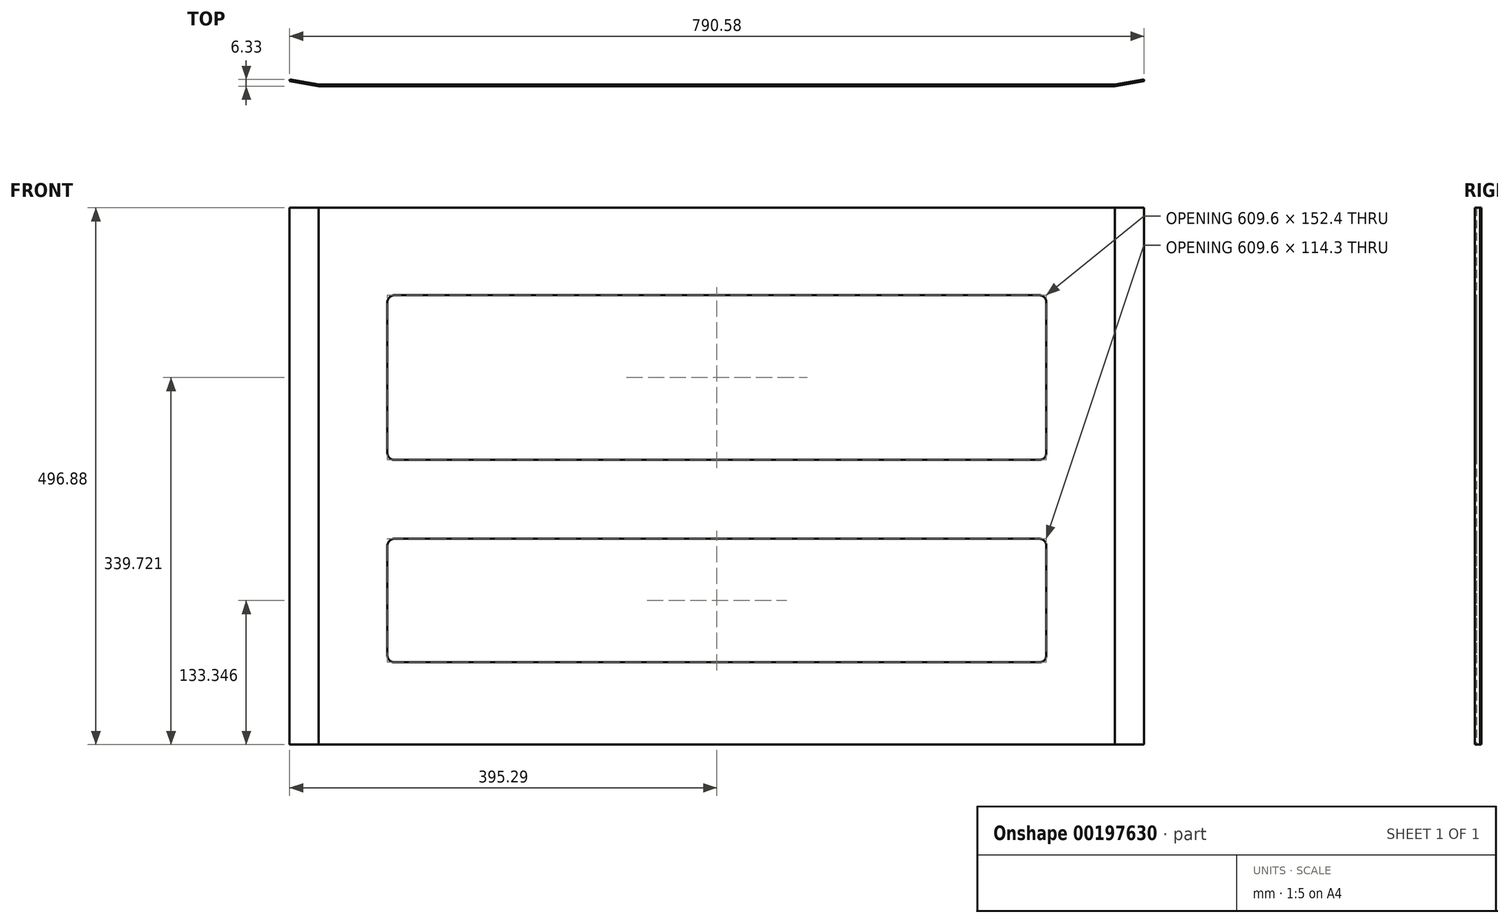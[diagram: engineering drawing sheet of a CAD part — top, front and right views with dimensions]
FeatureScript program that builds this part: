
annotation { "Feature Type Name" : "Feature", "Feature Type Description" : "" }
export const myFeature = defineFeature(function(context is Context, id is Id, definition is map)
    precondition{}
    {
        {
            var Q0;
            Q0=qCreatedBy(makeId("Front.planeOp"),FACE);
            var sketch = newSketch(context, id + "F0", { "sketchPlane" : qUnion([Q0])});
            skLineSegment(sketch, "E0.bottom", {"start": v(395.29, 248.44) * mm, "end": v(-395.29, 248.44) * mm});
            skLineSegment(sketch, "E0.top", {"start": v(395.29, -248.44) * mm, "end": v(-395.29, -248.44) * mm});
            skLineSegment(sketch, "E0.left", {"start": v(395.29, 248.44) * mm, "end": v(395.29, -248.44) * mm});
            skLineSegment(sketch, "E0.right", {"start": v(-395.29, 248.44) * mm, "end": v(-395.29, -248.44) * mm});
            skPoint(sketch, "E0.middle", {"position": v(0, 0) * mm});
            skLineSegment(sketch, "E1.bottom", {"start": v(298.45, 167.48) * mm, "end": v(-298.45, 167.48) * mm});
            skLineSegment(sketch, "E1.top", {"start": v(298.45, 15.08) * mm, "end": v(-298.45, 15.08) * mm});
            skLineSegment(sketch, "E1.left", {"start": v(304.8, 161.13) * mm, "end": v(304.8, 21.43) * mm});
            skLineSegment(sketch, "E1.right", {"start": v(-304.8, 161.13) * mm, "end": v(-304.8, 21.43) * mm});
            skPoint(sketch, "E1.middle", {"position": v(0, 91.28) * mm});
            skLineSegment(sketch, "E2.bottom", {"start": v(298.45, -57.94) * mm, "end": v(-298.45, -57.94) * mm});
            skLineSegment(sketch, "E2.top", {"start": v(298.45, -172.24) * mm, "end": v(-298.45, -172.24) * mm});
            skLineSegment(sketch, "E2.left", {"start": v(304.8, -64.3) * mm, "end": v(304.8, -165.9) * mm});
            skLineSegment(sketch, "E2.right", {"start": v(-304.8, -64.3) * mm, "end": v(-304.8, -165.9) * mm});
            skPoint(sketch, "E2.middle", {"position": v(0, -115.1) * mm});
            skPoint(sketch, "E3.visualSharp", {"position": v(304.8, 167.48) * mm});
            skArc(sketch, "E3.filletArc", {"start": v(304.8, 161.13) * mm, "mid": v(302.94, 165.62) * mm, "end": v(298.45, 167.48) * mm});
            skPoint(sketch, "E4.visualSharp", {"position": v(-304.8, 167.48) * mm});
            skArc(sketch, "E4.filletArc", {"start": v(-298.45, 167.48) * mm, "mid": v(-302.94, 165.62) * mm, "end": v(-304.8, 161.13) * mm});
            skPoint(sketch, "E5.visualSharp", {"position": v(-304.8, 15.08) * mm});
            skArc(sketch, "E5.filletArc", {"start": v(-304.8, 21.43) * mm, "mid": v(-302.94, 16.94) * mm, "end": v(-298.45, 15.08) * mm});
            skPoint(sketch, "E6.visualSharp", {"position": v(304.8, 15.08) * mm});
            skArc(sketch, "E6.filletArc", {"start": v(298.45, 15.08) * mm, "mid": v(302.94, 16.94) * mm, "end": v(304.8, 21.43) * mm});
            skPoint(sketch, "E7.visualSharp", {"position": v(304.8, -57.94) * mm});
            skArc(sketch, "E7.filletArc", {"start": v(304.8, -64.3) * mm, "mid": v(302.94, -59.8) * mm, "end": v(298.45, -57.94) * mm});
            skPoint(sketch, "E8.visualSharp", {"position": v(304.8, -172.24) * mm});
            skArc(sketch, "E8.filletArc", {"start": v(298.45, -172.24) * mm, "mid": v(302.94, -170.38) * mm, "end": v(304.8, -165.9) * mm});
            skPoint(sketch, "E9.visualSharp", {"position": v(-304.8, -57.94) * mm});
            skArc(sketch, "E9.filletArc", {"start": v(-298.45, -57.94) * mm, "mid": v(-302.94, -59.8) * mm, "end": v(-304.8, -64.3) * mm});
            skPoint(sketch, "E10.visualSharp", {"position": v(-304.8, -172.24) * mm});
            skArc(sketch, "E10.filletArc", {"start": v(-304.8, -165.9) * mm, "mid": v(-302.94, -170.38) * mm, "end": v(-298.45, -172.24) * mm});
            skSolve(sketch);
        }
        {
            var Q0;
            Q0=makeQuery(id+"F0.imprint","IMPRINT",FACE,{"disambiguationData":[TD([[makeQuery(id+"F0.imprint","IMPRINT",EDGE,{"derivedFrom":sQuery(id+"F0.wireOp",EDGE,"E0.bottom")}),1.0]])]});
            extrude(context, id + "F1", {"entities" : qUnion([Q0]), "oppositeDirection" : true, "depth" : 76.2 * mm, "offsetDistance" : 25.4 * mm});
        }
        {
            var Q0;
            Q0=makeQuery(id+"F1.opExtrude","CAP_EDGE",EDGE,{"disambiguationData":[OSD([sQuery(id+"F0.wireOp",EDGE,"E0.right")])],"isStart":true});
            var Q1;
            Q1=makeQuery(id+"F1.opExtrude","CAP_EDGE",EDGE,{"disambiguationData":[OSD([sQuery(id+"F0.wireOp",EDGE,"E0.left")])],"isStart":true});
            chamfer(context, id + "F2", {"entities" : qUnion([Q0, Q1]), "chamferType" : ChamferType.TWO_OFFSETS, "width1" : 26.99 * mm, "oppositeDirection" : false, "width2" : 4.76 * mm, "tangentPropagation" : true});
        }
        {
            var Q0;
            Q0=qCreatedBy(makeId("Top.planeOp"),FACE);
            var sketch = newSketch(context, id + "F3", { "sketchPlane" : qUnion([Q0])});
            skLineSegment(sketch, "E11", {"start": v(-368.3, 0) * mm, "end": v(-395.29, 4.76) * mm});
            skLineSegment(sketch, "E12", {"start": v(-395.29, 4.76) * mm, "end": v(-395.01, 6.33) * mm});
            skLineSegment(sketch, "E13", {"start": v(-395.01, 6.33) * mm, "end": v(-368.16, 1.59) * mm});
            skLineSegment(sketch, "E14", {"start": v(-368.16, 1.59) * mm, "end": v(368.16, 1.59) * mm});
            skLineSegment(sketch, "E15", {"start": v(0, 129) * mm, "end": v(0, -158.19) * mm, "construction": true});
            skLineSegment(sketch, "E16.MirrorCS", {"start": v(395.01, 6.33) * mm, "end": v(368.16, 1.59) * mm});
            skLineSegment(sketch, "E17.MirrorCS", {"start": v(395.29, 4.76) * mm, "end": v(395.01, 6.33) * mm});
            skLineSegment(sketch, "E18.MirrorCS", {"start": v(368.3, 0) * mm, "end": v(395.29, 4.76) * mm});
            skLineSegment(sketch, "E19", {"start": v(-368.3, 0) * mm, "end": v(368.3, 0) * mm});
            skSolve(sketch);
        }
        {
            var Q0;
            Q0 = qSketchRegion(id + "F3", true);
            extrude(context, id + "F4", {"entities" : qUnion([Q0]), "operationType" : NewBodyOperationType.INTERSECT, "endBound" : BoundingType.THROUGH_ALL, "depth" : 25.4 * mm, "offsetDistance" : 25.4 * mm, "hasSecondDirection" : true, "secondDirectionBound" : BoundingType.THROUGH_ALL, "secondDirectionOppositeDirection" : true, "secondDirectionDepth" : 25.4 * mm});
        }
    });
